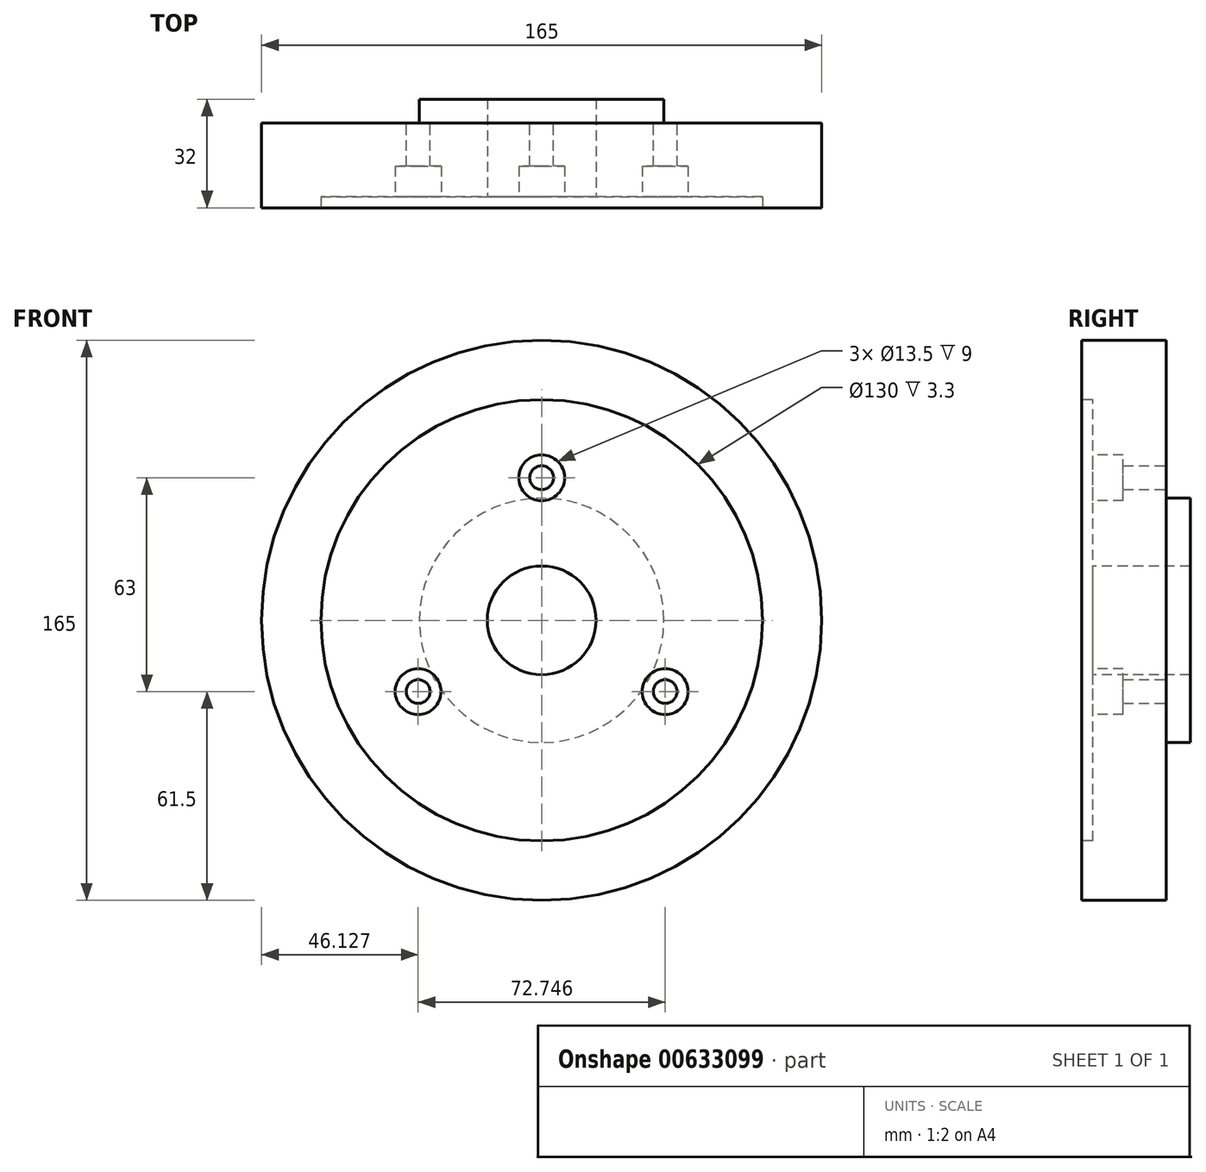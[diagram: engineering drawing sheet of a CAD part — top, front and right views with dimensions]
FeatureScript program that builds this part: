
annotation { "Feature Type Name" : "Feature", "Feature Type Description" : "" }
export const myFeature = defineFeature(function(context is Context, id is Id, definition is map)
    precondition{}
    {
        {
            var Q0;
            Q0=qCreatedBy(makeId("Right.planeOp"),FACE);
            var sketch = newSketch(context, id + "F0", { "sketchPlane" : qUnion([Q0])});
            skLineSegment(sketch, "E0", {"start": v(32, 16) * mm, "end": v(32, 36) * mm, "construction": true});
            skLineSegment(sketch, "E1", {"start": v(32, 16) * mm, "end": v(32, 36) * mm});
            skLineSegment(sketch, "E2", {"start": v(32, 36) * mm, "end": v(25, 36) * mm});
            skLineSegment(sketch, "E3", {"start": v(25, 36) * mm, "end": v(25, 82.5) * mm});
            skLineSegment(sketch, "E4", {"start": v(25, 82.5) * mm, "end": v(0, 82.5) * mm});
            skLineSegment(sketch, "E5", {"start": v(0, 82.5) * mm, "end": v(0, 65) * mm});
            skLineSegment(sketch, "E6", {"start": v(0, 65) * mm, "end": v(3.3, 65) * mm});
            skLineSegment(sketch, "E7", {"start": v(3.3, 65) * mm, "end": v(3.3, 16) * mm});
            skLineSegment(sketch, "E8", {"start": v(3.3, 16) * mm, "end": v(32, 16) * mm});
            skLineSegment(sketch, "E9", {"start": v(0, 0) * mm, "end": v(43.45, 0) * mm, "construction": true});
            skSolve(sketch);
        }
        {
            var Q0;
            Q0=makeQuery(id+"F0.imprint","IMPRINT",FACE,{"disambiguationData":[TD([[makeQuery(id+"F0.imprint","IMPRINT",EDGE,{"derivedFrom":sQuery(id+"F0.wireOp",EDGE,"E1")}),1.0]])]});
            var Q1;
            Q1=sQuery(id+"F0.wireOp",EDGE,"E9");
            revolve(context, id + "F1", {"entities" : qUnion([Q0]), "axis" : qUnion([Q1]), "revolveType" : RevolveType.FULL});
        }
        {
            var Q0;
            Q0=makeQuery(id+"F1.opRevolve","SWEPT_FACE",FACE,{"disambiguationData":[OSD([sQuery(id+"F0.wireOp",EDGE,"E7")])]});
            var sketch = newSketch(context, id + "F2", { "sketchPlane" : qUnion([Q0])});
            skCircle(sketch, "E10", {"center": v(0, 42) * mm, "radius": 6.75 * mm});
            skCircle(sketch, "E11.1.0", {"center": v(-36.37, -21) * mm, "radius": 6.75 * mm});
            skCircle(sketch, "E11.2.0", {"center": v(36.37, -21) * mm, "radius": 6.75 * mm});
            skPoint(sketch, "E11.center", {"position": v(0, 0) * mm});
            skSolve(sketch);
        }
        {
            var Q0;
            Q0=makeQuery(id+"F2.imprint","IMPRINT",FACE,{"disambiguationData":[TD([[makeQuery(id+"F2.imprint","IMPRINT",EDGE,{"derivedFrom":sQuery(id+"F2.wireOp",EDGE,"E10")}),1.0]])]});
            var Q1;
            Q1=makeQuery(id+"F2.imprint","IMPRINT",FACE,{"disambiguationData":[TD([[makeQuery(id+"F2.imprint","IMPRINT",EDGE,{"derivedFrom":sQuery(id+"F2.wireOp",EDGE,"E11.2.0")}),1.0]])]});
            var Q2;
            Q2=makeQuery(id+"F2.imprint","IMPRINT",FACE,{"disambiguationData":[TD([[makeQuery(id+"F2.imprint","IMPRINT",EDGE,{"derivedFrom":sQuery(id+"F2.wireOp",EDGE,"E11.1.0")}),1.0]])]});
            extrude(context, id + "F3", {"entities" : qUnion([Q0, Q1, Q2]), "operationType" : NewBodyOperationType.REMOVE, "oppositeDirection" : true, "depth" : 9 * mm, "offsetDistance" : 25 * mm});
        }
        {
            var Q0;
            Q0=makeQuery(id+"F1.opRevolve","SWEPT_FACE",FACE,{"disambiguationData":[OSD([sQuery(id+"F0.wireOp",EDGE,"E3")])]});
            var sketch = newSketch(context, id + "F4", { "sketchPlane" : qUnion([Q0])});
            skCircle(sketch, "E12", {"center": v(0, 42) * mm, "radius": 3.5 * mm});
            skCircle(sketch, "E13.1.0", {"center": v(-36.37, -21) * mm, "radius": 3.5 * mm});
            skCircle(sketch, "E13.2.0", {"center": v(36.37, -21) * mm, "radius": 3.5 * mm});
            skPoint(sketch, "E13.center", {"position": v(0, 0) * mm});
            skSolve(sketch);
        }
        {
            var Q0;
            Q0=makeQuery(id+"F4.imprint","IMPRINT",FACE,{"disambiguationData":[TD([[makeQuery(id+"F4.imprint","IMPRINT",EDGE,{"derivedFrom":sQuery(id+"F4.wireOp",EDGE,"E12")}),1.0]])]});
            var Q1;
            Q1=makeQuery(id+"F4.imprint","IMPRINT",FACE,{"disambiguationData":[TD([[makeQuery(id+"F4.imprint","IMPRINT",EDGE,{"derivedFrom":sQuery(id+"F4.wireOp",EDGE,"E13.1.0")}),1.0]])]});
            var Q2;
            Q2=makeQuery(id+"F4.imprint","IMPRINT",FACE,{"disambiguationData":[TD([[makeQuery(id+"F4.imprint","IMPRINT",EDGE,{"derivedFrom":sQuery(id+"F4.wireOp",EDGE,"E13.2.0")}),1.0]])]});
            extrude(context, id + "F5", {"entities" : qUnion([Q0, Q1, Q2]), "operationType" : NewBodyOperationType.REMOVE, "endBound" : BoundingType.THROUGH_ALL, "oppositeDirection" : true, "depth" : 25 * mm, "offsetDistance" : 25 * mm});
        }
    });
